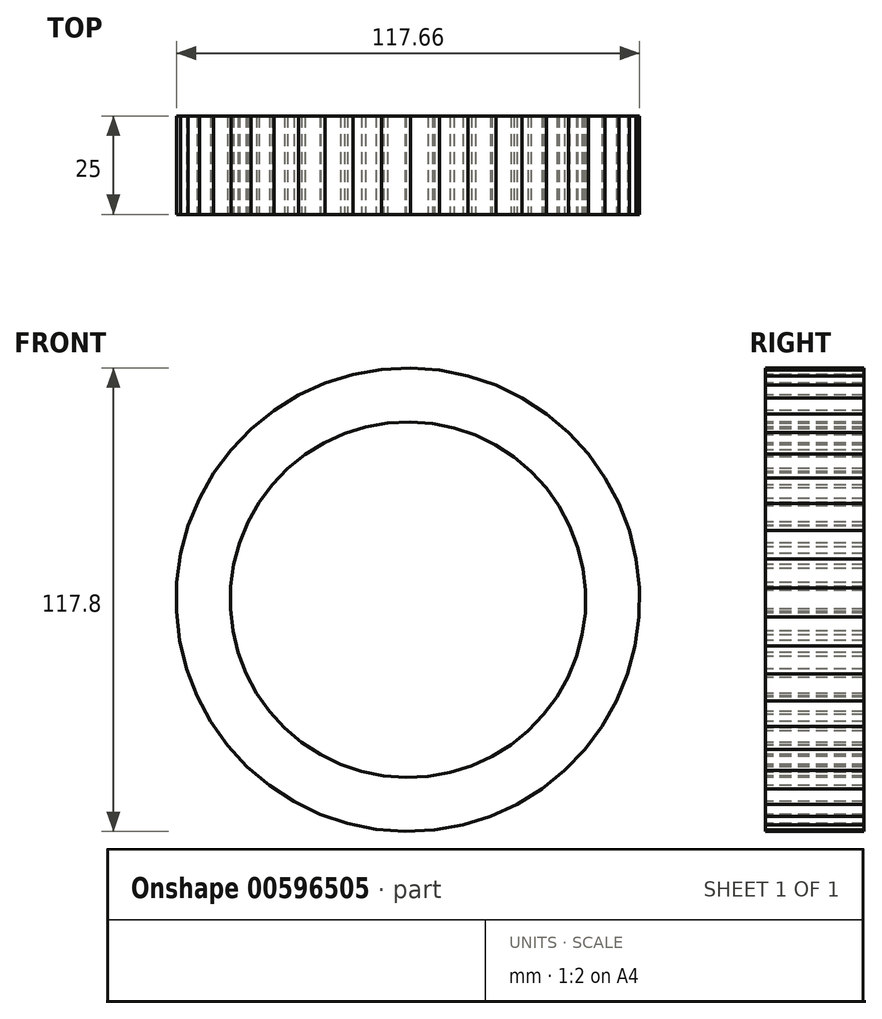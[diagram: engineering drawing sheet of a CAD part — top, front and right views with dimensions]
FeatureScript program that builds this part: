
annotation { "Feature Type Name" : "Feature", "Feature Type Description" : "" }
export const myFeature = defineFeature(function(context is Context, id is Id, definition is map)
    precondition{}
    {
        {
            var Q0;
            Q0=qCreatedBy(makeId("Front.planeOp"),FACE);
            var sketch = newSketch(context, id + "F0", { "sketchPlane" : qUnion([Q0])});
            skCircle(sketch, "E0.cCircle", {"center": v(0, 0) * mm, "radius": 45.09 * mm, "construction": true});
            skLineSegment(sketch, "E0.0", {"start": v(31.31, 32.56) * mm, "end": v(35.15, 28.38) * mm});
            skLineSegment(sketch, "E0.1", {"start": v(35.15, 28.38) * mm, "end": v(38.43, 23.75) * mm});
            skLineSegment(sketch, "E0.2", {"start": v(38.43, 23.75) * mm, "end": v(41.1, 18.75) * mm});
            skLineSegment(sketch, "E0.3", {"start": v(41.1, 18.75) * mm, "end": v(43.13, 13.45) * mm});
            skLineSegment(sketch, "E0.4", {"start": v(43.13, 13.45) * mm, "end": v(44.47, 7.94) * mm});
            skLineSegment(sketch, "E0.5", {"start": v(44.47, 7.94) * mm, "end": v(45.12, 2.3) * mm});
            skLineSegment(sketch, "E0.6", {"start": v(45.12, 2.3) * mm, "end": v(45.05, -3.37) * mm});
            skLineSegment(sketch, "E0.7", {"start": v(45.05, -3.37) * mm, "end": v(44.27, -8.99) * mm});
            skLineSegment(sketch, "E0.8", {"start": v(44.27, -8.99) * mm, "end": v(42.8, -14.47) * mm});
            skLineSegment(sketch, "E0.9", {"start": v(42.8, -14.47) * mm, "end": v(40.65, -19.72) * mm});
            skLineSegment(sketch, "E0.10", {"start": v(40.65, -19.72) * mm, "end": v(37.85, -24.65) * mm});
            skLineSegment(sketch, "E0.11", {"start": v(37.85, -24.65) * mm, "end": v(34.47, -29.2) * mm});
            skLineSegment(sketch, "E0.12", {"start": v(34.47, -29.2) * mm, "end": v(30.53, -33.3) * mm});
            skLineSegment(sketch, "E0.13", {"start": v(30.53, -33.3) * mm, "end": v(26.12, -36.86) * mm});
            skLineSegment(sketch, "E0.14", {"start": v(26.12, -36.86) * mm, "end": v(21.3, -39.84) * mm});
            skLineSegment(sketch, "E0.15", {"start": v(21.3, -39.84) * mm, "end": v(16.13, -42.2) * mm});
            skLineSegment(sketch, "E0.16", {"start": v(16.13, -42.2) * mm, "end": v(10.72, -43.89) * mm});
            skLineSegment(sketch, "E0.17", {"start": v(10.72, -43.89) * mm, "end": v(5.13, -44.88) * mm});
            skLineSegment(sketch, "E0.18", {"start": v(5.13, -44.88) * mm, "end": v(-0.53, -45.17) * mm});
            skLineSegment(sketch, "E0.19", {"start": v(-0.53, -45.17) * mm, "end": v(-6.2, -44.75) * mm});
            skLineSegment(sketch, "E0.20", {"start": v(-6.2, -44.75) * mm, "end": v(-11.75, -43.62) * mm});
            skLineSegment(sketch, "E0.21", {"start": v(-11.75, -43.62) * mm, "end": v(-17.12, -41.8) * mm});
            skLineSegment(sketch, "E0.22", {"start": v(-17.12, -41.8) * mm, "end": v(-22.23, -39.33) * mm});
            skLineSegment(sketch, "E0.23", {"start": v(-22.23, -39.33) * mm, "end": v(-26.98, -36.23) * mm});
            skLineSegment(sketch, "E0.24", {"start": v(-26.98, -36.23) * mm, "end": v(-31.31, -32.56) * mm});
            skLineSegment(sketch, "E0.25", {"start": v(-31.31, -32.56) * mm, "end": v(-35.15, -28.38) * mm});
            skLineSegment(sketch, "E0.26", {"start": v(-35.15, -28.38) * mm, "end": v(-38.43, -23.75) * mm});
            skLineSegment(sketch, "E0.27", {"start": v(-38.43, -23.75) * mm, "end": v(-41.1, -18.75) * mm});
            skLineSegment(sketch, "E0.28", {"start": v(-41.1, -18.75) * mm, "end": v(-43.13, -13.45) * mm});
            skLineSegment(sketch, "E0.29", {"start": v(-43.13, -13.45) * mm, "end": v(-44.47, -7.94) * mm});
            skLineSegment(sketch, "E0.30", {"start": v(-44.47, -7.94) * mm, "end": v(-45.12, -2.3) * mm});
            skLineSegment(sketch, "E0.31", {"start": v(-45.12, -2.3) * mm, "end": v(-45.05, 3.37) * mm});
            skLineSegment(sketch, "E0.32", {"start": v(-45.05, 3.37) * mm, "end": v(-44.27, 8.99) * mm});
            skLineSegment(sketch, "E0.33", {"start": v(-44.27, 8.99) * mm, "end": v(-42.8, 14.47) * mm});
            skLineSegment(sketch, "E0.34", {"start": v(-42.8, 14.47) * mm, "end": v(-40.65, 19.72) * mm});
            skLineSegment(sketch, "E0.35", {"start": v(-40.65, 19.72) * mm, "end": v(-37.85, 24.65) * mm});
            skLineSegment(sketch, "E0.36", {"start": v(-37.85, 24.65) * mm, "end": v(-34.47, 29.2) * mm});
            skLineSegment(sketch, "E0.37", {"start": v(-34.47, 29.2) * mm, "end": v(-30.53, 33.3) * mm});
            skLineSegment(sketch, "E0.38", {"start": v(-30.53, 33.3) * mm, "end": v(-26.12, 36.86) * mm});
            skLineSegment(sketch, "E0.39", {"start": v(-26.12, 36.86) * mm, "end": v(-21.3, 39.84) * mm});
            skLineSegment(sketch, "E0.40", {"start": v(-21.3, 39.84) * mm, "end": v(-16.13, 42.2) * mm});
            skLineSegment(sketch, "E0.41", {"start": v(-16.13, 42.2) * mm, "end": v(-10.72, 43.89) * mm});
            skLineSegment(sketch, "E0.42", {"start": v(-10.72, 43.89) * mm, "end": v(-5.13, 44.88) * mm});
            skLineSegment(sketch, "E0.43", {"start": v(-5.13, 44.88) * mm, "end": v(0.53, 45.17) * mm});
            skLineSegment(sketch, "E0.44", {"start": v(0.53, 45.17) * mm, "end": v(6.2, 44.75) * mm});
            skLineSegment(sketch, "E0.45", {"start": v(6.2, 44.75) * mm, "end": v(11.75, 43.62) * mm});
            skLineSegment(sketch, "E0.46", {"start": v(11.75, 43.62) * mm, "end": v(17.12, 41.8) * mm});
            skLineSegment(sketch, "E0.47", {"start": v(17.12, 41.8) * mm, "end": v(22.23, 39.33) * mm});
            skLineSegment(sketch, "E0.48", {"start": v(22.23, 39.33) * mm, "end": v(26.98, 36.23) * mm});
            skLineSegment(sketch, "E0.49", {"start": v(26.98, 36.23) * mm, "end": v(31.31, 32.56) * mm});
            skPoint(sketch, "E0.0.midPoint", {"position": v(33.23, 30.47) * mm});
            skLineSegment(sketch, "E1.0", {"start": v(15.32, 56.87) * mm, "end": v(22.33, 54.5) * mm});
            skLineSegment(sketch, "E1.1", {"start": v(8.07, 58.35) * mm, "end": v(15.32, 56.87) * mm});
            skLineSegment(sketch, "E1.2", {"start": v(0.7, 58.9) * mm, "end": v(8.07, 58.35) * mm});
            skLineSegment(sketch, "E1.3", {"start": v(-6.7, 58.52) * mm, "end": v(0.7, 58.9) * mm});
            skLineSegment(sketch, "E1.4", {"start": v(6.7, -58.52) * mm, "end": v(-0.7, -58.9) * mm});
            skLineSegment(sketch, "E1.5", {"start": v(13.97, -57.22) * mm, "end": v(6.7, -58.52) * mm});
            skLineSegment(sketch, "E1.6", {"start": v(21.04, -55.02) * mm, "end": v(13.97, -57.22) * mm});
            skLineSegment(sketch, "E1.7", {"start": v(27.77, -51.95) * mm, "end": v(21.04, -55.02) * mm});
            skLineSegment(sketch, "E1.8", {"start": v(34.06, -48.06) * mm, "end": v(27.77, -51.95) * mm});
            skLineSegment(sketch, "E1.9", {"start": v(39.81, -43.41) * mm, "end": v(34.06, -48.06) * mm});
            skLineSegment(sketch, "E1.10", {"start": v(44.94, -38.08) * mm, "end": v(39.81, -43.41) * mm});
            skLineSegment(sketch, "E1.11", {"start": v(49.36, -32.15) * mm, "end": v(44.94, -38.08) * mm});
            skLineSegment(sketch, "E1.12", {"start": v(53, -25.7) * mm, "end": v(49.36, -32.15) * mm});
            skLineSegment(sketch, "E1.13", {"start": v(55.8, -18.86) * mm, "end": v(53, -25.7) * mm});
            skLineSegment(sketch, "E1.14", {"start": v(57.72, -11.72) * mm, "end": v(55.8, -18.86) * mm});
            skLineSegment(sketch, "E1.15", {"start": v(58.74, -4.4) * mm, "end": v(57.72, -11.72) * mm});
            skLineSegment(sketch, "E1.16", {"start": v(40.83, 42.46) * mm, "end": v(45.82, 37) * mm});
            skLineSegment(sketch, "E1.17", {"start": v(35.18, 47.24) * mm, "end": v(40.83, 42.46) * mm});
            skLineSegment(sketch, "E1.18", {"start": v(28.98, 51.28) * mm, "end": v(35.18, 47.24) * mm});
            skLineSegment(sketch, "E1.19", {"start": v(22.33, 54.5) * mm, "end": v(28.98, 51.28) * mm});
            skLineSegment(sketch, "E1.20", {"start": v(45.82, 37) * mm, "end": v(50.1, 30.97) * mm});
            skLineSegment(sketch, "E1.21", {"start": v(50.1, 30.97) * mm, "end": v(53.59, 24.45) * mm});
            skLineSegment(sketch, "E1.22", {"start": v(53.59, 24.45) * mm, "end": v(56.23, 17.54) * mm});
            skLineSegment(sketch, "E1.23", {"start": v(56.23, 17.54) * mm, "end": v(57.98, 10.35) * mm});
            skLineSegment(sketch, "E1.24", {"start": v(57.98, 10.35) * mm, "end": v(58.83, 3) * mm});
            skLineSegment(sketch, "E1.25", {"start": v(58.83, 3) * mm, "end": v(58.74, -4.4) * mm});
            skLineSegment(sketch, "E1.26", {"start": v(-0.7, -58.9) * mm, "end": v(-8.07, -58.35) * mm});
            skLineSegment(sketch, "E1.27", {"start": v(-8.07, -58.35) * mm, "end": v(-15.32, -56.87) * mm});
            skLineSegment(sketch, "E1.28", {"start": v(-15.32, -56.87) * mm, "end": v(-22.33, -54.5) * mm});
            skLineSegment(sketch, "E1.29", {"start": v(-22.33, -54.5) * mm, "end": v(-28.98, -51.28) * mm});
            skLineSegment(sketch, "E1.30", {"start": v(-28.98, -51.28) * mm, "end": v(-35.18, -47.24) * mm});
            skLineSegment(sketch, "E1.31", {"start": v(-35.18, -47.24) * mm, "end": v(-40.83, -42.46) * mm});
            skLineSegment(sketch, "E1.32", {"start": v(-40.83, -42.46) * mm, "end": v(-45.82, -37) * mm});
            skLineSegment(sketch, "E1.33", {"start": v(-45.82, -37) * mm, "end": v(-50.1, -30.97) * mm});
            skLineSegment(sketch, "E1.34", {"start": v(-50.1, -30.97) * mm, "end": v(-53.59, -24.45) * mm});
            skLineSegment(sketch, "E1.35", {"start": v(-53.59, -24.45) * mm, "end": v(-56.23, -17.54) * mm});
            skLineSegment(sketch, "E1.36", {"start": v(-56.23, -17.54) * mm, "end": v(-57.98, -10.35) * mm});
            skLineSegment(sketch, "E1.37", {"start": v(-57.98, -10.35) * mm, "end": v(-58.83, -3) * mm});
            skLineSegment(sketch, "E1.38", {"start": v(-58.83, -3) * mm, "end": v(-58.74, 4.4) * mm});
            skLineSegment(sketch, "E1.39", {"start": v(-58.74, 4.4) * mm, "end": v(-57.72, 11.72) * mm});
            skLineSegment(sketch, "E1.40", {"start": v(-57.72, 11.72) * mm, "end": v(-55.8, 18.86) * mm});
            skLineSegment(sketch, "E1.41", {"start": v(-55.8, 18.86) * mm, "end": v(-53, 25.7) * mm});
            skLineSegment(sketch, "E1.42", {"start": v(-53, 25.7) * mm, "end": v(-49.36, 32.15) * mm});
            skLineSegment(sketch, "E1.43", {"start": v(-49.36, 32.15) * mm, "end": v(-44.94, 38.08) * mm});
            skLineSegment(sketch, "E1.44", {"start": v(-44.94, 38.08) * mm, "end": v(-39.81, 43.41) * mm});
            skLineSegment(sketch, "E1.45", {"start": v(-39.81, 43.41) * mm, "end": v(-34.06, 48.06) * mm});
            skLineSegment(sketch, "E1.46", {"start": v(-34.06, 48.06) * mm, "end": v(-27.77, 51.95) * mm});
            skLineSegment(sketch, "E1.47", {"start": v(-27.77, 51.95) * mm, "end": v(-21.04, 55.02) * mm});
            skLineSegment(sketch, "E1.48", {"start": v(-21.04, 55.02) * mm, "end": v(-13.97, 57.22) * mm});
            skLineSegment(sketch, "E1.49", {"start": v(-13.97, 57.22) * mm, "end": v(-6.7, 58.52) * mm});
            skSolve(sketch);
        }
        {
            var Q0;
            Q0=sQuery(id+"F0.wireOp",EDGE,"E1.1");
            var Q1;
            Q1=sQuery(id+"F0.wireOp",EDGE,"E1.39");
            var Q2;
            Q2=sQuery(id+"F0.wireOp",EDGE,"E0.25");
            var Q3;
            Q3=sQuery(id+"F0.wireOp",EDGE,"E0.41");
            var Q4;
            Q4=sQuery(id+"F0.wireOp",EDGE,"E1.7");
            var Q5;
            Q5=sQuery(id+"F0.wireOp",EDGE,"E1.49");
            var Q6;
            Q6=sQuery(id+"F0.wireOp",EDGE,"E1.42");
            var Q7;
            Q7=sQuery(id+"F0.wireOp",EDGE,"E1.23");
            var Q8;
            Q8=sQuery(id+"F0.wireOp",EDGE,"E0.18");
            var Q9;
            Q9=sQuery(id+"F0.wireOp",EDGE,"E1.32");
            var Q10;
            Q10=sQuery(id+"F0.wireOp",EDGE,"E1.16");
            var Q11;
            Q11=sQuery(id+"F0.wireOp",EDGE,"E1.0");
            var Q12;
            Q12=sQuery(id+"F0.wireOp",EDGE,"E0.34");
            var Q13;
            Q13=sQuery(id+"F0.wireOp",EDGE,"E0.43");
            var Q14;
            Q14=sQuery(id+"F0.wireOp",EDGE,"E1.9");
            var Q15;
            Q15=sQuery(id+"F0.wireOp",EDGE,"E0.27");
            var Q16;
            Q16=sQuery(id+"F0.wireOp",EDGE,"E1.25");
            var Q17;
            Q17=sQuery(id+"F0.wireOp",EDGE,"E1.41");
            var Q18;
            Q18=sQuery(id+"F0.wireOp",EDGE,"E0.20");
            var Q19;
            Q19=sQuery(id+"F0.wireOp",EDGE,"E1.48");
            var Q20;
            Q20=sQuery(id+"F0.wireOp",EDGE,"E1.34");
            var Q21;
            Q21=sQuery(id+"F0.wireOp",EDGE,"E1.11");
            var Q22;
            Q22=sQuery(id+"F0.wireOp",EDGE,"E1.27");
            var Q23;
            Q23=sQuery(id+"F0.wireOp",EDGE,"E1.18");
            var Q24;
            Q24=sQuery(id+"F0.wireOp",EDGE,"E0.45");
            var Q25;
            Q25=sQuery(id+"F0.wireOp",EDGE,"E1.2");
            var Q26;
            Q26=sQuery(id+"F0.wireOp",EDGE,"E0.29");
            var Q27;
            Q27=sQuery(id+"F0.wireOp",EDGE,"E0.36");
            var Q28;
            Q28=sQuery(id+"F0.wireOp",EDGE,"E1.8");
            var Q29;
            Q29=sQuery(id+"F0.wireOp",EDGE,"E0.42");
            var Q30;
            Q30=sQuery(id+"F0.wireOp",EDGE,"E0.26");
            var Q31;
            Q31=sQuery(id+"F0.wireOp",EDGE,"E1.40");
            var Q32;
            Q32=sQuery(id+"F0.wireOp",EDGE,"E1.24");
            var Q33;
            Q33=sQuery(id+"F0.wireOp",EDGE,"E0.19");
            var Q34;
            Q34=sQuery(id+"F0.wireOp",EDGE,"E1.26");
            var Q35;
            Q35=sQuery(id+"F0.wireOp",EDGE,"E1.33");
            var Q36;
            Q36=sQuery(id+"F0.wireOp",EDGE,"E1.17");
            var Q37;
            Q37=sQuery(id+"F0.wireOp",EDGE,"E1.43");
            var Q38;
            Q38=sQuery(id+"F0.wireOp",EDGE,"E1.10");
            var Q39;
            Q39=sQuery(id+"F0.wireOp",EDGE,"E0.44");
            var Q40;
            Q40=sQuery(id+"F0.wireOp",EDGE,"E0.35");
            var Q41;
            Q41=sQuery(id+"F0.wireOp",EDGE,"E0.28");
            var Q42;
            Q42=sQuery(id+"F0.wireOp",EDGE,"E0.21");
            var Q43;
            Q43=sQuery(id+"F0.wireOp",EDGE,"E1.28");
            var Q44;
            Q44=sQuery(id+"F0.wireOp",EDGE,"E1.35");
            var Q45;
            Q45=sQuery(id+"F0.wireOp",EDGE,"E1.12");
            var Q46;
            Q46=sQuery(id+"F0.wireOp",EDGE,"E1.19");
            var Q47;
            Q47=sQuery(id+"F0.wireOp",EDGE,"E1.3");
            var Q48;
            Q48=sQuery(id+"F0.wireOp",EDGE,"E0.46");
            var Q49;
            Q49=sQuery(id+"F0.wireOp",EDGE,"E0.30");
            var Q50;
            Q50=sQuery(id+"F0.wireOp",EDGE,"E0.37");
            var Q51;
            Q51=sQuery(id+"F0.wireOp",EDGE,"E1.44");
            var Q52;
            Q52=sQuery(id+"F0.wireOp",EDGE,"E0.12");
            var Q53;
            Q53=sQuery(id+"F0.wireOp",EDGE,"E0.13");
            var Q54;
            Q54=sQuery(id+"F0.wireOp",EDGE,"E0.14");
            var Q55;
            Q55=sQuery(id+"F0.wireOp",EDGE,"E0.1");
            var Q56;
            Q56=sQuery(id+"F0.wireOp",EDGE,"E0.2");
            var Q57;
            Q57=sQuery(id+"F0.wireOp",EDGE,"E0.3");
            var Q58;
            Q58=sQuery(id+"F0.wireOp",EDGE,"E0.4");
            var Q59;
            Q59=sQuery(id+"F0.wireOp",EDGE,"E0.5");
            var Q60;
            Q60=sQuery(id+"F0.wireOp",EDGE,"E0.6");
            var Q61;
            Q61=sQuery(id+"F0.wireOp",EDGE,"E0.7");
            var Q62;
            Q62=sQuery(id+"F0.wireOp",EDGE,"E0.8");
            var Q63;
            Q63=sQuery(id+"F0.wireOp",EDGE,"E0.9");
            var Q64;
            Q64=sQuery(id+"F0.wireOp",EDGE,"E0.10");
            var Q65;
            Q65=sQuery(id+"F0.wireOp",EDGE,"E0.11");
            var Q66;
            Q66=sQuery(id+"F0.wireOp",EDGE,"E1.45");
            var Q67;
            Q67=sQuery(id+"F0.wireOp",EDGE,"E1.4");
            var Q68;
            Q68=sQuery(id+"F0.wireOp",EDGE,"E0.38");
            var Q69;
            Q69=sQuery(id+"F0.wireOp",EDGE,"E0.22");
            var Q70;
            Q70=sQuery(id+"F0.wireOp",EDGE,"E1.36");
            var Q71;
            Q71=sQuery(id+"F0.wireOp",EDGE,"E1.20");
            var Q72;
            Q72=sQuery(id+"F0.wireOp",EDGE,"E0.15");
            var Q73;
            Q73=sQuery(id+"F0.wireOp",EDGE,"E1.29");
            var Q74;
            Q74=sQuery(id+"F0.wireOp",EDGE,"E1.13");
            var Q75;
            Q75=sQuery(id+"F0.wireOp",EDGE,"E0.47");
            var Q76;
            Q76=sQuery(id+"F0.wireOp",EDGE,"E0.31");
            var Q77;
            Q77=sQuery(id+"F0.wireOp",EDGE,"E1.5");
            var Q78;
            Q78=sQuery(id+"F0.wireOp",EDGE,"E0.39");
            var Q79;
            Q79=sQuery(id+"F0.wireOp",EDGE,"E0.23");
            var Q80;
            Q80=sQuery(id+"F0.wireOp",EDGE,"E1.37");
            var Q81;
            Q81=sQuery(id+"F0.wireOp",EDGE,"E1.21");
            var Q82;
            Q82=sQuery(id+"F0.wireOp",EDGE,"E0.16");
            var Q83;
            Q83=sQuery(id+"F0.wireOp",EDGE,"E1.30");
            var Q84;
            Q84=sQuery(id+"F0.wireOp",EDGE,"E1.14");
            var Q85;
            Q85=sQuery(id+"F0.wireOp",EDGE,"E0.48");
            var Q86;
            Q86=sQuery(id+"F0.wireOp",EDGE,"E0.32");
            var Q87;
            Q87=sQuery(id+"F0.wireOp",EDGE,"E1.46");
            var Q88;
            Q88=sQuery(id+"F0.wireOp",EDGE,"E1.6");
            var Q89;
            Q89=sQuery(id+"F0.wireOp",EDGE,"E0.40");
            var Q90;
            Q90=sQuery(id+"F0.wireOp",EDGE,"E0.24");
            var Q91;
            Q91=sQuery(id+"F0.wireOp",EDGE,"E1.38");
            var Q92;
            Q92=sQuery(id+"F0.wireOp",EDGE,"E1.22");
            var Q93;
            Q93=sQuery(id+"F0.wireOp",EDGE,"E0.17");
            var Q94;
            Q94=sQuery(id+"F0.wireOp",EDGE,"E1.31");
            var Q95;
            Q95=sQuery(id+"F0.wireOp",EDGE,"E1.15");
            var Q96;
            Q96=sQuery(id+"F0.wireOp",EDGE,"E0.49");
            var Q97;
            Q97=sQuery(id+"F0.wireOp",EDGE,"E0.33");
            var Q98;
            Q98=sQuery(id+"F0.wireOp",EDGE,"E1.47");
            var Q99;
            Q99=sQuery(id+"F0.wireOp",EDGE,"E0.0");
            extrude(context, id + "F1", {"bodyType" : ToolBodyType.SURFACE, "surfaceEntities" : qUnion([Q0, Q1, Q2, Q3, Q4, Q5, Q6, Q7, Q8, Q9, Q10, Q11, Q12, Q13, Q14, Q15, Q16, Q17, Q18, Q19, Q20, Q21, Q22, Q23, Q24, Q25, Q26, Q27, Q28, Q29, Q30, Q31, Q32, Q33, Q34, Q35, Q36, Q37, Q38, Q39, Q40, Q41, Q42, Q43, Q44, Q45, Q46, Q47, Q48, Q49, Q50, Q51, Q52, Q53, Q54, Q55, Q56, Q57, Q58, Q59, Q60, Q61, Q62, Q63, Q64, Q65, Q66, Q67, Q68, Q69, Q70, Q71, Q72, Q73, Q74, Q75, Q76, Q77, Q78, Q79, Q80, Q81, Q82, Q83, Q84, Q85, Q86, Q87, Q88, Q89, Q90, Q91, Q92, Q93, Q94, Q95, Q96, Q97, Q98, Q99]), "depth" : 25 * mm, "offsetDistance" : 25 * mm});
        }
    });
